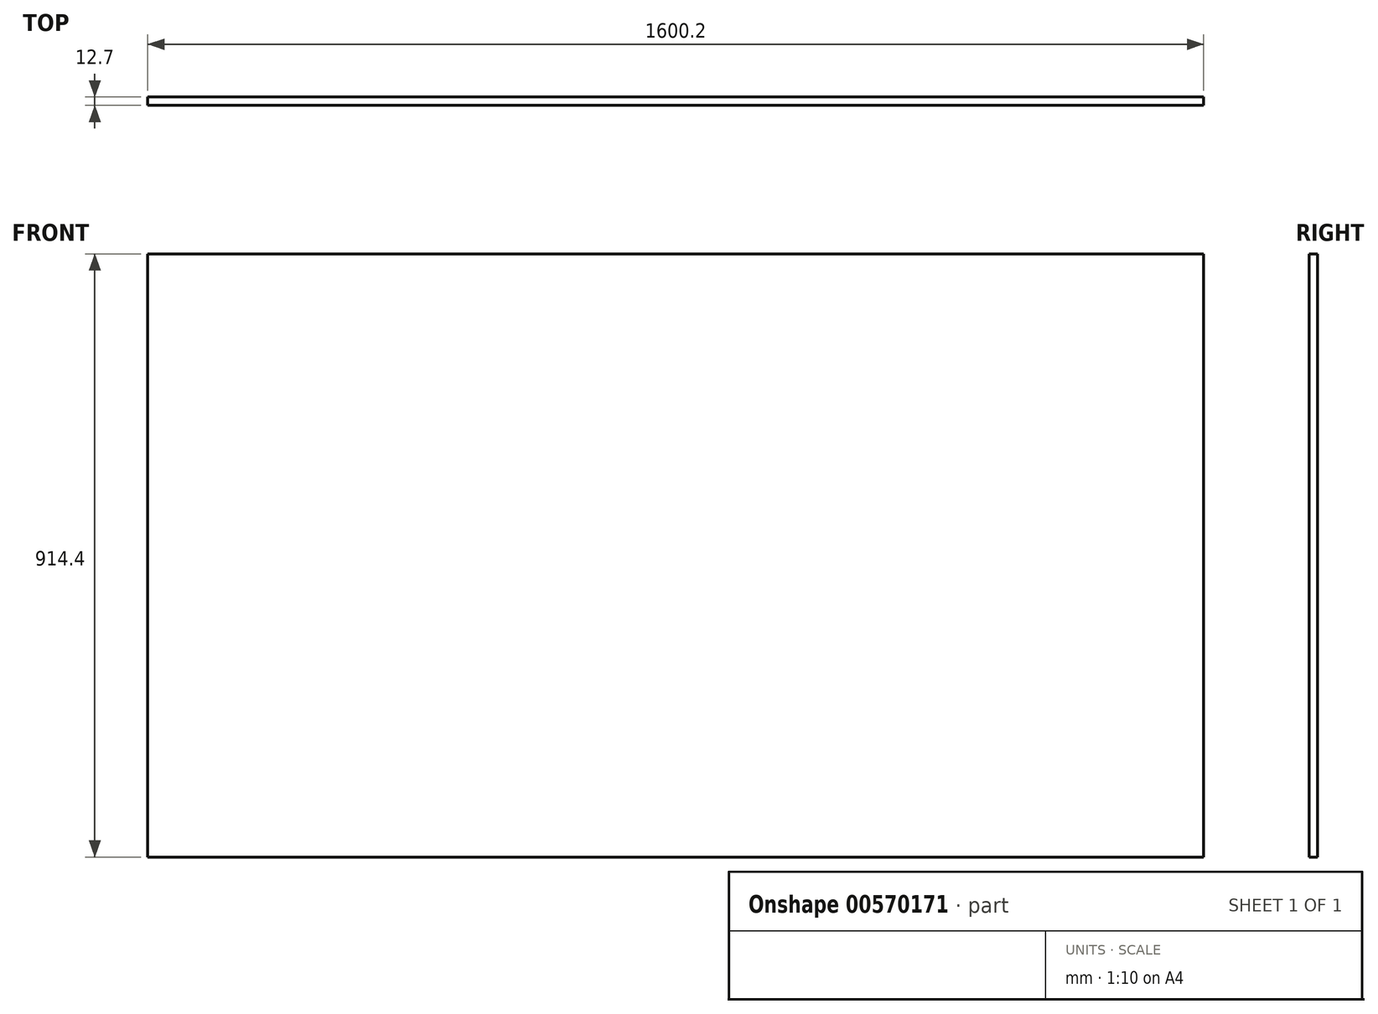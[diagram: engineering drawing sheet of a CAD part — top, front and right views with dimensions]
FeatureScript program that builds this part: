
annotation { "Feature Type Name" : "Feature", "Feature Type Description" : "" }
export const myFeature = defineFeature(function(context is Context, id is Id, definition is map)
    precondition{}
    {
        {
            var Q0;
            Q0=qCreatedBy(makeId("Front.planeOp"),FACE);
            var sketch = newSketch(context, id + "F0", { "sketchPlane" : qUnion([Q0])});
            skLineSegment(sketch, "E0.bottom", {"start": v(-909.4, -414.79) * mm, "end": v(690.8, -414.79) * mm});
            skLineSegment(sketch, "E0.top", {"start": v(-909.4, 499.61) * mm, "end": v(690.8, 499.61) * mm});
            skLineSegment(sketch, "E0.left", {"start": v(-909.4, -414.79) * mm, "end": v(-909.4, 499.61) * mm});
            skLineSegment(sketch, "E0.right", {"start": v(690.8, -414.79) * mm, "end": v(690.8, 499.61) * mm});
            skSolve(sketch);
        }
        {
            var Q0;
            Q0 = qSketchRegion(id + "F0", true);
            extrude(context, id + "F1", {"entities" : qUnion([Q0]), "depth" : 12.7 * mm, "offsetDistance" : 25.4 * mm});
        }
    });
